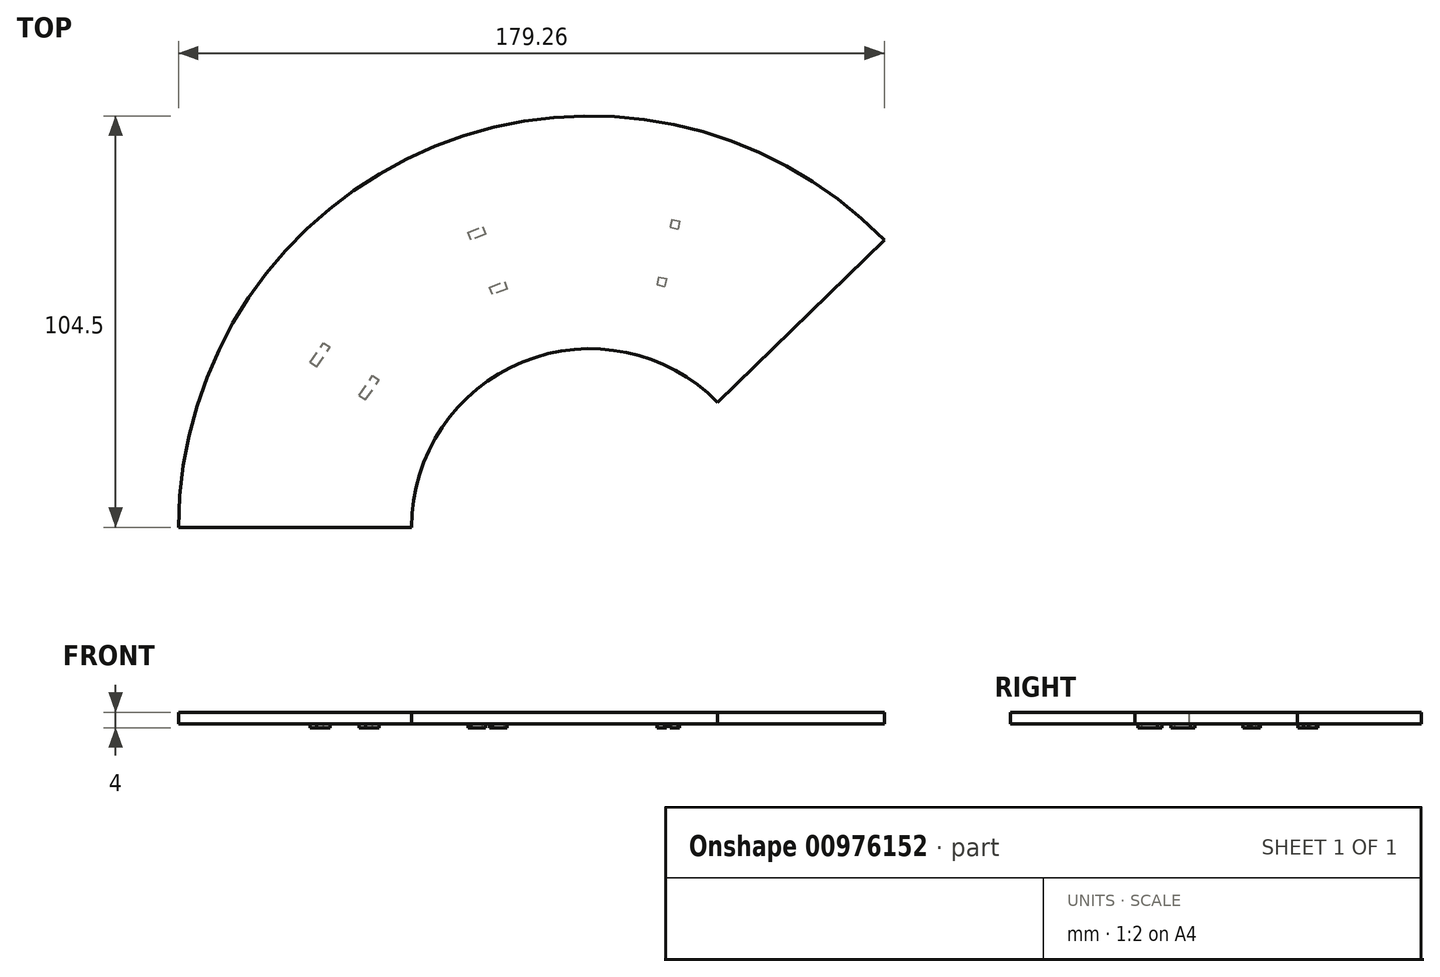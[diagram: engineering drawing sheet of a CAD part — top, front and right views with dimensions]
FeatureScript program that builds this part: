
annotation { "Feature Type Name" : "Feature", "Feature Type Description" : "" }
export const myFeature = defineFeature(function(context is Context, id is Id, definition is map)
    precondition{}
    {
        {
            var Q0;
            Q0=qCreatedBy(makeId("Top.planeOp"),FACE);
            var sketch = newSketch(context, id + "F0", { "sketchPlane" : qUnion([Q0])});
            skArc(sketch, "E0", {"start": v(74.76, 73.01) * mm, "mid": v(-39.42, 96.78) * mm, "end": v(-104.5, 0) * mm});
            skArc(sketch, "E1", {"start": v(32.44, 31.69) * mm, "mid": v(-17.1, 42) * mm, "end": v(-45.35, 0) * mm});
            skLineSegment(sketch, "E2", {"start": v(-45.35, 0) * mm, "end": v(-104.5, 0) * mm});
            skLineSegment(sketch, "E3", {"start": v(32.44, 31.69) * mm, "end": v(74.76, 73.01) * mm});
            skSolve(sketch);
        }
        {
            var Q0;
            Q0=qSketchRegion(id+"F0",true);
            extrude(context, id + "F1", {"entities" : qUnion([Q0]), "depth" : 3 * mm, "offsetDistance" : 25 * mm});
        }
        {
            var Q0;
            Q0=makeQuery(id+"F1.opExtrude","CAP_FACE",FACE,{"disambiguationData":[OSD([sQuery(id+"F0.wireOp",EDGE,"E0"),sQuery(id+"F0.wireOp",EDGE,"E1"),sQuery(id+"F0.wireOp",EDGE,"E2"),sQuery(id+"F0.wireOp",EDGE,"E3")])],"isStart":false});
            var sketch = newSketch(context, id + "F2", { "sketchPlane" : qUnion([Q0])});
            skLineSegment(sketch, "E4", {"start": v(-17.1, 42) * mm, "end": v(-39.42, 96.78) * mm});
            skLineSegment(sketch, "E5", {"start": v(-38.13, 24.55) * mm, "end": v(-87.2, 57.58) * mm});
            skLineSegment(sketch, "E6", {"start": v(10.49, 44.12) * mm, "end": v(22.52, 102.04) * mm});
            skLineSegment(sketch, "E7", {"start": v(-54.72, 35.71) * mm, "end": v(-55.84, 34.05) * mm});
            skLineSegment(sketch, "E8", {"start": v(-55.84, 34.05) * mm, "end": v(-57.5, 35.17) * mm});
            skLineSegment(sketch, "E9", {"start": v(-57.5, 35.17) * mm, "end": v(-56.38, 36.83) * mm});
            skLineSegment(sketch, "E10", {"start": v(-56.38, 36.83) * mm, "end": v(-55.27, 38.49) * mm});
            skLineSegment(sketch, "E11", {"start": v(-55.27, 38.49) * mm, "end": v(-53.6, 37.37) * mm});
            skLineSegment(sketch, "E12", {"start": v(-54.72, 35.71) * mm, "end": v(-53.6, 37.37) * mm});
            skLineSegment(sketch, "E13", {"start": v(-67.17, 44.09) * mm, "end": v(-68.29, 42.43) * mm});
            skLineSegment(sketch, "E14", {"start": v(-68.29, 42.43) * mm, "end": v(-69.94, 43.55) * mm});
            skLineSegment(sketch, "E15", {"start": v(-69.94, 43.55) * mm, "end": v(-68.83, 45.2) * mm});
            skLineSegment(sketch, "E16", {"start": v(-68.83, 45.2) * mm, "end": v(-67.71, 46.86) * mm});
            skLineSegment(sketch, "E17", {"start": v(-67.71, 46.86) * mm, "end": v(-66.05, 45.75) * mm});
            skLineSegment(sketch, "E18", {"start": v(-67.17, 44.09) * mm, "end": v(-66.05, 45.75) * mm});
            skLineSegment(sketch, "E19.1.0", {"start": v(-30.98, 74.88) * mm, "end": v(-29.12, 75.62) * mm});
            skLineSegment(sketch, "E19.1.1", {"start": v(-29.12, 75.62) * mm, "end": v(-27.26, 76.35) * mm});
            skLineSegment(sketch, "E19.1.2", {"start": v(-28.39, 73.76) * mm, "end": v(-26.53, 74.5) * mm});
            skLineSegment(sketch, "E19.1.3", {"start": v(-27.26, 76.35) * mm, "end": v(-26.53, 74.5) * mm});
            skLineSegment(sketch, "E19.1.4", {"start": v(-28.39, 73.76) * mm, "end": v(-30.25, 73.02) * mm});
            skLineSegment(sketch, "E19.1.5", {"start": v(-30.25, 73.02) * mm, "end": v(-30.98, 74.88) * mm});
            skLineSegment(sketch, "E19.1.6", {"start": v(-25.47, 60.93) * mm, "end": v(-23.6, 61.67) * mm});
            skLineSegment(sketch, "E19.1.7", {"start": v(-23.6, 61.67) * mm, "end": v(-21.75, 62.4) * mm});
            skLineSegment(sketch, "E19.1.8", {"start": v(-21.75, 62.4) * mm, "end": v(-21.01, 60.54) * mm});
            skLineSegment(sketch, "E19.1.9", {"start": v(-22.87, 59.8) * mm, "end": v(-21.01, 60.54) * mm});
            skLineSegment(sketch, "E19.1.10", {"start": v(-22.87, 59.8) * mm, "end": v(-24.73, 59.07) * mm});
            skLineSegment(sketch, "E19.1.11", {"start": v(-24.73, 59.07) * mm, "end": v(-25.47, 60.93) * mm});
            skLineSegment(sketch, "E19.2.1", {"start": v(20.83, 78.2) * mm, "end": v(22.78, 77.75) * mm});
            skLineSegment(sketch, "E19.2.2", {"start": v(20.38, 76.25) * mm, "end": v(22.33, 75.8) * mm});
            skLineSegment(sketch, "E19.2.3", {"start": v(22.78, 77.75) * mm, "end": v(22.33, 75.8) * mm});
            skLineSegment(sketch, "E19.2.7", {"start": v(17.47, 63.58) * mm, "end": v(19.42, 63.13) * mm});
            skLineSegment(sketch, "E19.2.8", {"start": v(19.42, 63.13) * mm, "end": v(18.97, 61.18) * mm});
            skLineSegment(sketch, "E19.2.9", {"start": v(17.02, 61.63) * mm, "end": v(18.97, 61.18) * mm});
            skPoint(sketch, "E19.center", {"position": v(0, -3.52) * mm});
            skLineSegment(sketch, "E19.anchor1", {"start": v(0, -3.52) * mm, "end": v(-69.94, 43.55) * mm, "construction": true});
            skLineSegment(sketch, "E19.anchor2", {"start": v(0, -3.52) * mm, "end": v(18.51, 77.06) * mm, "construction": true});
            skLineSegment(sketch, "E20", {"start": v(17.47, 63.58) * mm, "end": v(17.02, 61.63) * mm});
            skLineSegment(sketch, "E21", {"start": v(20.83, 78.2) * mm, "end": v(20.38, 76.25) * mm});
            skLineSegment(sketch, "E22", {"start": v(-68.29, 42.43) * mm, "end": v(-69.4, 40.77) * mm});
            skLineSegment(sketch, "E23", {"start": v(-69.4, 40.77) * mm, "end": v(-71.06, 41.89) * mm});
            skLineSegment(sketch, "E24", {"start": v(-71.06, 41.89) * mm, "end": v(-69.94, 43.55) * mm});
            skLineSegment(sketch, "E25", {"start": v(-57.5, 35.17) * mm, "end": v(-58.62, 33.51) * mm});
            skLineSegment(sketch, "E26", {"start": v(-58.62, 33.51) * mm, "end": v(-56.96, 32.4) * mm});
            skLineSegment(sketch, "E27", {"start": v(-56.96, 32.4) * mm, "end": v(-55.84, 34.05) * mm});
            skSolve(sketch);
        }
        {
            var Q0;
            Q0=qSketchRegion(id+"F2",true);
            extrude(context, id + "F3", {"entities" : qUnion([Q0]), "operationType" : NewBodyOperationType.ADD, "oppositeDirection" : true, "depth" : 4 * mm, "offsetDistance" : 25 * mm});
        }
    });
